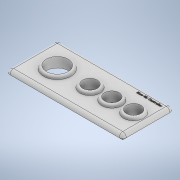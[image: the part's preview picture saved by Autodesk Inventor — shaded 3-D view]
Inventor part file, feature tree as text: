
AUTODESK INVENTOR PART (.ipt)
format: ipt  version: 2021 (Build 250183000, 183)  size: 755,712 bytes
history: native  units: in
note: dims shown in document units (in); Inventor stores cm internally (conversion verified against a paired STEP export)
features: extrude x9, sketch x9, fillet x3
ambient origin geometry x8: Origin, YZ Plane, XZ Plane, XY Plane, X Axis, Y Axis, Z Axis, Center Point
bodies: Solid1 (feature_tree)
feature tree (21):
  extrude  "Extrusion1"  Depth=2.3622in
  extrude  "Extrusion2"  Depth=0.1969in TaperAngle=0.0deg
  extrude  "Extrusion3"  Depth=0.1969in TaperAngle=0.0deg
  extrude  "Extrusion4"  Depth=1.1811in
  extrude  "Extrusion5"  Depth=1.1811in
  extrude  "Extrusion6"  Depth=1.1811in
  extrude  "Extrusion7"  Depth=0.7874in
  extrude  "Extrusion8"  Depth=0.1476in
  fillet  "Fillet1"  Radius=0.1476in
  fillet  "Fillet2"  Radius=0.1476in
  fillet  "Fillet3"  Radius=0.1476in
  extrude  "Extrusion9"  Depth=0.1476in
  sketch  "Sketch1"  dims[d0=5.9055in d1=2.3622in]
  sketch  "Sketch2"  dims[d2=0.3937in d3=0.0in d4=0.1969in d5=0.0in]
  sketch  "Sketch3"  dims[d6=0.1969in d7=0.0in d8=0.1969in d9=0.0in]
  sketch  "Sketch4"  dims[d10=0.1969in d11=0.0in d14=1.1811in]
  sketch  "Sketch5"  dims[d15=0.3937in d16=0.0in d17=1.1811in]
  sketch  "Sketch6"  dims[d19=1.1811in d21=1.1811in]
  sketch  "Sketch7"  dims[d22=2.3622in d23=0.7874in]
  sketch  "Sketch8"  dims[d24=0.3937in d25=0.0in d26=0.1476in d27=0.1476in d28=0.1476in d29=0.1476in]
  sketch  "Sketch9"  dims[d30=0.1476in d31=0.0in d32=0.1476in d33=0.1969in d34=0.1969in d35=0.0197in d36=0.0in]
